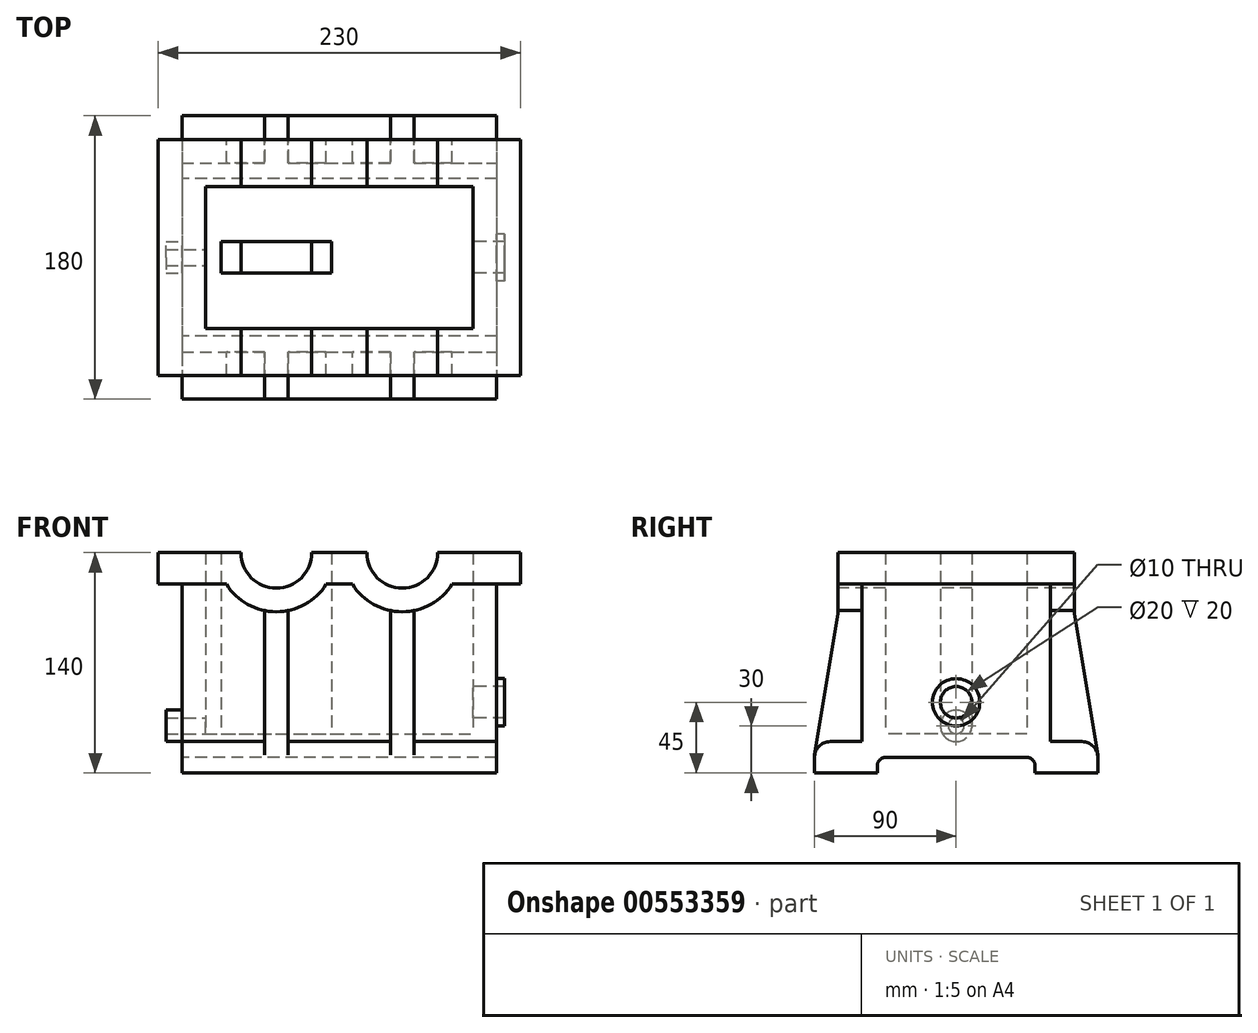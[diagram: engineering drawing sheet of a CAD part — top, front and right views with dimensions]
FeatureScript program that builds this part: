
annotation { "Feature Type Name" : "Feature", "Feature Type Description" : "" }
export const myFeature = defineFeature(function(context is Context, id is Id, definition is map)
    precondition{}
    {
        {
            var Q0;
            Q0=qCreatedBy(makeId("Top.planeOp"),FACE);
            var sketch = newSketch(context, id + "F0", { "sketchPlane" : qUnion([Q0])});
            skLineSegment(sketch, "E0.bottom", {"start": v(-100, 60) * mm, "end": v(100, 60) * mm});
            skLineSegment(sketch, "E0.top", {"start": v(-100, -60) * mm, "end": v(100, -60) * mm});
            skLineSegment(sketch, "E0.left", {"start": v(-100, 60) * mm, "end": v(-100, -60) * mm});
            skLineSegment(sketch, "E0.right", {"start": v(100, 60) * mm, "end": v(100, -60) * mm});
            skPoint(sketch, "E0.middle", {"position": v(0, 0) * mm});
            skSolve(sketch);
        }
        {
            var Q0;
            Q0=makeQuery(id+"F0.imprint","IMPRINT",FACE,{"disambiguationData":[TD([[makeQuery(id+"F0.imprint","IMPRINT",EDGE,{"derivedFrom":sQuery(id+"F0.wireOp",EDGE,"E0.bottom")}),-1.0]])]});
            extrude(context, id + "F1", {"entities" : qUnion([Q0]), "depth" : 100 * mm, "offsetDistance" : 25 * mm});
        }
        {
            var Q0;
            Q0=makeQuery(id+"F1.opExtrude","CAP_FACE",FACE,{"disambiguationData":[OSD([sQuery(id+"F0.wireOp",EDGE,"E0.bottom"),sQuery(id+"F0.wireOp",EDGE,"E0.top"),sQuery(id+"F0.wireOp",EDGE,"E0.left"),sQuery(id+"F0.wireOp",EDGE,"E0.right")])],"isStart":false});
            shell(context, id + "F2", {"entities" : qUnion([Q0]), "thickness" : 15 * mm});
        }
        {
            var Q0;
            Q0=makeQuery(id+"F1.opExtrude","CAP_FACE",FACE,{"disambiguationData":[OSD([sQuery(id+"F0.wireOp",EDGE,"E0.bottom"),sQuery(id+"F0.wireOp",EDGE,"E0.top"),sQuery(id+"F0.wireOp",EDGE,"E0.left"),sQuery(id+"F0.wireOp",EDGE,"E0.right")])],"isStart":false});
            var sketch = newSketch(context, id + "F3", { "sketchPlane" : qUnion([Q0])});
            skLineSegment(sketch, "E1.bottom", {"start": v(-115, 75) * mm, "end": v(115, 75) * mm});
            skLineSegment(sketch, "E1.top", {"start": v(-115, -75) * mm, "end": v(115, -75) * mm});
            skLineSegment(sketch, "E1.left", {"start": v(-115, 75) * mm, "end": v(-115, -75) * mm});
            skLineSegment(sketch, "E1.right", {"start": v(115, 75) * mm, "end": v(115, -75) * mm});
            skPoint(sketch, "E1.middle", {"position": v(0, 0) * mm});
            skLineSegment(sketch, "E2.0", {"start": v(-85, 45) * mm, "end": v(85, 45) * mm});
            skLineSegment(sketch, "E3.0", {"start": v(85, 45) * mm, "end": v(85, -45) * mm});
            skLineSegment(sketch, "E4.0", {"start": v(-85, -45) * mm, "end": v(85, -45) * mm});
            skLineSegment(sketch, "E5.0", {"start": v(-85, 45) * mm, "end": v(-85, -45) * mm});
            skSolve(sketch);
        }
        {
            var Q0;
            Q0 = qSketchRegion(id + "F3", true);
            extrude(context, id + "F4", {"entities" : qUnion([Q0]), "operationType" : NewBodyOperationType.ADD, "depth" : 20 * mm, "offsetDistance" : 25 * mm});
        }
        {
            var Q0;
            Q0=makeQuery(id+"F1.opExtrude","CAP_FACE",FACE,{"disambiguationData":[OSD([sQuery(id+"F0.wireOp",EDGE,"E0.bottom"),sQuery(id+"F0.wireOp",EDGE,"E0.top"),sQuery(id+"F0.wireOp",EDGE,"E0.left"),sQuery(id+"F0.wireOp",EDGE,"E0.right")])],"isStart":true});
            var sketch = newSketch(context, id + "F5", { "sketchPlane" : qUnion([Q0])});
            skLineSegment(sketch, "E6.bottom", {"start": v(-100, -90) * mm, "end": v(100, -90) * mm});
            skLineSegment(sketch, "E6.top", {"start": v(-100, 90) * mm, "end": v(100, 90) * mm});
            skLineSegment(sketch, "E6.left", {"start": v(-100, -90) * mm, "end": v(-100, 90) * mm});
            skLineSegment(sketch, "E6.right", {"start": v(100, -90) * mm, "end": v(100, 90) * mm});
            skPoint(sketch, "E6.middle", {"position": v(0, 0) * mm});
            skSolve(sketch);
        }
        {
            var Q0;
            Q0 = qSketchRegion(id + "F5", true);
            extrude(context, id + "F6", {"entities" : qUnion([Q0]), "operationType" : NewBodyOperationType.ADD, "depth" : 20 * mm, "offsetDistance" : 25 * mm});
        }
        {
            var Q0;
            Q0=makeQuery(id+"F6.boolean.opBoolean","MERGE",FACE,{"derivedFrom":[makeQuery(id+"F1.opExtrude","SWEPT_FACE",FACE,{"disambiguationData":[OSD([sQuery(id+"F0.wireOp",EDGE,"E0.left")])]}),makeQuery(id+"F6.opExtrude","SWEPT_FACE",FACE,{"disambiguationData":[OSD([sQuery(id+"F5.wireOp",EDGE,"E6.left")])]})]});
            var sketch = newSketch(context, id + "F7", { "sketchPlane" : qUnion([Q0])});
            skLineSegment(sketch, "E7.bottom", {"start": v(-50, -10) * mm, "end": v(50, -10) * mm});
            skLineSegment(sketch, "E7.top", {"start": v(-50, -20) * mm, "end": v(50, -20) * mm});
            skLineSegment(sketch, "E7.left", {"start": v(-50, -10) * mm, "end": v(-50, -20) * mm});
            skLineSegment(sketch, "E7.right", {"start": v(50, -10) * mm, "end": v(50, -20) * mm});
            skSolve(sketch);
        }
        {
            var Q0;
            Q0=makeQuery(id+"F7.imprint","IMPRINT",FACE,{"disambiguationData":[TD([[makeQuery(id+"F7.imprint","IMPRINT",EDGE,{"derivedFrom":sQuery(id+"F7.wireOp",EDGE,"E7.bottom")}),-1.0]])]});
            extrude(context, id + "F8", {"entities" : qUnion([Q0]), "operationType" : NewBodyOperationType.REMOVE, "oppositeDirection" : true, "depth" : 200 * mm, "offsetDistance" : 25 * mm});
        }
        {
            var Q0;
            Q0=makeQuery(id+"F8.boolean.opBoolean","COPY",EDGE,{"derivedFrom":makeQuery(id+"F8.opExtrude","SWEPT_EDGE",EDGE,{"disambiguationData":[OSD([sQuery(id+"F7.wireOp",EDGE,"E7.bottom"),sQuery(id+"F7.wireOp",EDGE,"E7.right")])]})});
            var Q1;
            Q1=makeQuery(id+"F8.boolean.opBoolean","COPY",EDGE,{"derivedFrom":makeQuery(id+"F8.opExtrude","SWEPT_EDGE",EDGE,{"disambiguationData":[OSD([sQuery(id+"F7.wireOp",EDGE,"E7.bottom"),sQuery(id+"F7.wireOp",EDGE,"E7.left")])]})});
            fillet(context, id + "F9", {"entities" : qUnion([Q0, Q1]), "radius" : 5 * mm, "tangentPropagation" : true, "allowEdgeOverflow" : false});
        }
        {
            var Q0;
            Q0=qCreatedBy(makeId("Front.planeOp"),FACE);
            var sketch = newSketch(context, id + "F10", { "sketchPlane" : qUnion([Q0])});
            skArc(sketch, "E8", {"start": v(-77.5, 120) * mm, "mid": v(-40, 82.5) * mm, "end": v(-2.5, 120) * mm});
            skArc(sketch, "E9", {"start": v(2.5, 120) * mm, "mid": v(40, 82.5) * mm, "end": v(77.5, 120) * mm});
            skLineSegment(sketch, "E10.0", {"start": v(-77.5, 120) * mm, "end": v(-2.5, 120) * mm});
            skPoint(sketch, "E11.orphan", {"position": v(-115, 120) * mm});
            skLineSegment(sketch, "E12.trimOffspring", {"start": v(2.5, 120) * mm, "end": v(77.5, 120) * mm});
            skPoint(sketch, "E13.orphan", {"position": v(115, 120) * mm});
            skSolve(sketch);
        }
        {
            var Q0;
            Q0 = qSketchRegion(id + "F10", true);
            var Q1;
            Q1=makeQuery(id+"F4.opExtrude","SWEPT_FACE",FACE,{"disambiguationData":[OSD([sQuery(id+"F3.wireOp",EDGE,"E1.top")])]});
            var Q2;
            Q2=makeQuery(id+"F4.opExtrude","SWEPT_FACE",FACE,{"disambiguationData":[OSD([sQuery(id+"F3.wireOp",EDGE,"E1.bottom")])]});
            extrude(context, id + "F11", {"entities" : qUnion([Q0]), "operationType" : NewBodyOperationType.ADD, "endBound" : BoundingType.UP_TO_SURFACE, "depth" : 25 * mm, "endBoundEntityFace" : qUnion([Q1]), "offsetDistance" : 25 * mm, "hasSecondDirection" : true, "secondDirectionBound" : SecondDirectionBoundingType.UP_TO_SURFACE, "secondDirectionOppositeDirection" : true, "secondDirectionDepth" : 25 * mm, "secondDirectionBoundEntityFace" : qUnion([Q2])});
        }
        {
            var Q0;
            Q0 = qSketchRegion(id + "F10", true);
            var Q1;
            Q1=makeQuery(id+"F4.boolean.opBoolean","MERGE",FACE,{"derivedFrom":[makeQuery(id+"F2.opShell","OFFSET_FACE",FACE,{"disambiguationData":[OSD([sQuery(id+"F0.wireOp",EDGE,"E0.top")])]}),makeQuery(id+"F4.opExtrude","SWEPT_FACE",FACE,{"disambiguationData":[OSD([sQuery(id+"F3.wireOp",EDGE,"E4.0")])]})]});
            var Q2;
            Q2=makeQuery(id+"F4.boolean.opBoolean","MERGE",FACE,{"derivedFrom":[makeQuery(id+"F2.opShell","OFFSET_FACE",FACE,{"disambiguationData":[OSD([sQuery(id+"F0.wireOp",EDGE,"E0.bottom")])]}),makeQuery(id+"F4.opExtrude","SWEPT_FACE",FACE,{"disambiguationData":[OSD([sQuery(id+"F3.wireOp",EDGE,"E2.0")])]})]});
            extrude(context, id + "F12", {"entities" : qUnion([Q0]), "operationType" : NewBodyOperationType.REMOVE, "endBound" : BoundingType.UP_TO_SURFACE, "depth" : 25 * mm, "endBoundEntityFace" : qUnion([Q1]), "offsetDistance" : 25 * mm, "hasSecondDirection" : true, "secondDirectionBound" : SecondDirectionBoundingType.UP_TO_SURFACE, "secondDirectionOppositeDirection" : true, "secondDirectionDepth" : 25 * mm, "secondDirectionBoundEntityFace" : qUnion([Q2])});
        }
        {
            var Q0;
            Q0=qCreatedBy(makeId("Front.planeOp"),FACE);
            var sketch = newSketch(context, id + "F13", { "sketchPlane" : qUnion([Q0])});
            skCircle(sketch, "E14", {"center": v(-40, 120) * mm, "radius": 22.5 * mm});
            skCircle(sketch, "E15", {"center": v(40, 120) * mm, "radius": 22.5 * mm});
            skSolve(sketch);
        }
        {
            var Q0;
            Q0 = qSketchRegion(id + "F13", true);
            extrude(context, id + "F14", {"entities" : qUnion([Q0]), "operationType" : NewBodyOperationType.REMOVE, "oppositeDirection" : true, "depth" : 200 * mm, "offsetDistance" : 25 * mm, "hasSecondDirection" : true, "secondDirectionOppositeDirection" : false, "secondDirectionDepth" : 200 * mm});
        }
        {
            var Q0;
            Q0=makeQuery(id+"F6.opExtrude","CAP_EDGE",EDGE,{"disambiguationData":[OSD([sQuery(id+"F5.wireOp",EDGE,"E6.top")])],"isStart":true});
            var Q1;
            Q1=makeQuery(id+"F6.opExtrude","CAP_EDGE",EDGE,{"disambiguationData":[OSD([sQuery(id+"F5.wireOp",EDGE,"E6.bottom")])],"isStart":true});
            fillet(context, id + "F15", {"entities" : qUnion([Q0, Q1]), "radius" : 10 * mm, "tangentPropagation" : true, "allowEdgeOverflow" : false});
        }
        {
            var Q0;
            Q0=qCreatedBy(makeId("Right.planeOp"),FACE);
            cPlane(context, id + "F16", {"entities" : qUnion([Q0]), "cplaneType" : CPlaneType.OFFSET, "offset" : 40 * mm, "width" : 150 * mm, "height" : 150 * mm});
        }
        {
            var Q0;
            Q0=qCreatedBy(makeId("Right.planeOp"),FACE);
            cPlane(context, id + "F17", {"entities" : qUnion([Q0]), "cplaneType" : CPlaneType.OFFSET, "offset" : 40 * mm, "oppositeDirection" : true, "width" : 150 * mm, "height" : 150 * mm});
        }
        {
            var Q0;
            Q0=qCreatedBy(id+"F16.planeOp",FACE);
            var sketch = newSketch(context, id + "F18", { "sketchPlane" : qUnion([Q0])});
            skLineSegment(sketch, "E16", {"start": v(72.14, 100) * mm, "end": v(89.87, -8.39) * mm});
            skLineSegment(sketch, "E17", {"start": v(60, -8.39) * mm, "end": v(60, 100) * mm});
            skLineSegment(sketch, "E18", {"start": v(60, 100) * mm, "end": v(72.14, 100) * mm});
            skLineSegment(sketch, "E19", {"start": v(60, -8.39) * mm, "end": v(89.87, -8.39) * mm});
            skLineSegment(sketch, "E20", {"start": v(60, 82.5) * mm, "end": v(75, 82.5) * mm});
            skLineSegment(sketch, "E21", {"start": v(0, 162.85) * mm, "end": v(0, -102.85) * mm, "construction": true});
            skLineSegment(sketch, "E22.MirrorCS", {"start": v(-72.14, 100) * mm, "end": v(-89.87, -8.39) * mm});
            skLineSegment(sketch, "E23.MirrorCS", {"start": v(-60, -8.39) * mm, "end": v(-89.87, -8.39) * mm});
            skLineSegment(sketch, "E24.MirrorCS", {"start": v(-60, -8.39) * mm, "end": v(-60, 100) * mm});
            skLineSegment(sketch, "E25.MirrorCS", {"start": v(-60, 100) * mm, "end": v(-72.14, 100) * mm});
            skSolve(sketch);
        }
        {
            var Q0;
            Q0 = qSketchRegion(id + "F18", true);
            extrude(context, id + "F19", {"entities" : qUnion([Q0]), "operationType" : NewBodyOperationType.ADD, "depth" : 7.5 * mm, "offsetDistance" : 25 * mm, "hasSecondDirection" : true, "secondDirectionOppositeDirection" : true, "secondDirectionDepth" : 7.5 * mm});
        }
        {
            var Q0;
            Q0=qCreatedBy(id+"F17.planeOp",FACE);
            var sketch = newSketch(context, id + "F20", { "sketchPlane" : qUnion([Q0])});
            skLineSegment(sketch, "E26.0", {"start": v(72.14, 100) * mm, "end": v(89.87, -8.39) * mm});
            skLineSegment(sketch, "E27.0", {"start": v(60, 100) * mm, "end": v(72.14, 100) * mm});
            skLineSegment(sketch, "E28.0", {"start": v(60, -8.39) * mm, "end": v(60, 100) * mm});
            skLineSegment(sketch, "E29.0", {"start": v(60, -8.39) * mm, "end": v(89.87, -8.39) * mm});
            skLineSegment(sketch, "E30.0", {"start": v(-60, -8.39) * mm, "end": v(-89.87, -8.39) * mm});
            skLineSegment(sketch, "E31.0", {"start": v(-60, -8.39) * mm, "end": v(-60, 100) * mm});
            skLineSegment(sketch, "E32.0", {"start": v(-72.14, 100) * mm, "end": v(-89.87, -8.39) * mm});
            skLineSegment(sketch, "E33.0", {"start": v(-60, 100) * mm, "end": v(-72.14, 100) * mm});
            skSolve(sketch);
        }
        {
            var Q0;
            Q0 = qSketchRegion(id + "F20", true);
            extrude(context, id + "F21", {"entities" : qUnion([Q0]), "operationType" : NewBodyOperationType.ADD, "depth" : 7.5 * mm, "offsetDistance" : 25 * mm, "hasSecondDirection" : true, "secondDirectionOppositeDirection" : true, "secondDirectionDepth" : 7.5 * mm});
        }
        {
            var Q0;
            Q0 = qSketchRegion(id + "F13", true);
            extrude(context, id + "F22", {"entities" : qUnion([Q0]), "operationType" : NewBodyOperationType.REMOVE, "oppositeDirection" : true, "depth" : 200 * mm, "offsetDistance" : 25 * mm, "hasSecondDirection" : true, "secondDirectionOppositeDirection" : false, "secondDirectionDepth" : 200 * mm});
        }
        {
            var Q0;
            Q0=makeQuery(id+"F2.opShell","OFFSET_FACE",FACE,{"disambiguationData":[OSD([sQuery(id+"F0.wireOp",EDGE,"E0.bottom"),sQuery(id+"F0.wireOp",EDGE,"E0.top"),sQuery(id+"F0.wireOp",EDGE,"E0.left"),sQuery(id+"F0.wireOp",EDGE,"E0.right")])]});
            extrude(context, id + "F23", {"entities" : qUnion([Q0]), "operationType" : NewBodyOperationType.REMOVE, "oppositeDirection" : true, "depth" : 10 * mm, "offsetDistance" : 25 * mm});
        }
        {
            var Q0;
            Q0=makeQuery(id+"F6.boolean.opBoolean","MERGE",FACE,{"derivedFrom":[makeQuery(id+"F1.opExtrude","SWEPT_FACE",FACE,{"disambiguationData":[OSD([sQuery(id+"F0.wireOp",EDGE,"E0.left")])]}),makeQuery(id+"F6.opExtrude","SWEPT_FACE",FACE,{"disambiguationData":[OSD([sQuery(id+"F5.wireOp",EDGE,"E6.left")])]})]});
            var sketch = newSketch(context, id + "F24", { "sketchPlane" : qUnion([Q0])});
            skCircle(sketch, "E34", {"center": v(0, 10) * mm, "radius": 5 * mm});
            skCircle(sketch, "E35", {"center": v(0, 10) * mm, "radius": 10 * mm});
            skLineSegment(sketch, "E36.0", {"start": v(-45, 5) * mm, "end": v(45, 5) * mm, "construction": true});
            skSolve(sketch);
        }
        {
            var Q0;
            Q0 = qSketchRegion(id + "F24", true);
            extrude(context, id + "F25", {"entities" : qUnion([Q0]), "operationType" : NewBodyOperationType.ADD, "depth" : 10 * mm, "offsetDistance" : 25 * mm});
        }
        {
            var Q0;
            Q0=makeQuery(id+"F25.boolean.opBoolean","SPLIT",FACE,{"disambiguationData":[TD([makeQuery(id+"F25.opExtrude","SWEPT_FACE",FACE,{"disambiguationData":[OSD([sQuery(id+"F24.wireOp",EDGE,"E34")])]})])],"derivedFrom":makeQuery(id+"F6.boolean.opBoolean","MERGE",FACE,{"derivedFrom":[makeQuery(id+"F1.opExtrude","SWEPT_FACE",FACE,{"disambiguationData":[OSD([sQuery(id+"F0.wireOp",EDGE,"E0.left")])]}),makeQuery(id+"F6.opExtrude","SWEPT_FACE",FACE,{"disambiguationData":[OSD([sQuery(id+"F5.wireOp",EDGE,"E6.left")])]})]})});
            extrude(context, id + "F26", {"entities" : qUnion([Q0]), "operationType" : NewBodyOperationType.REMOVE, "oppositeDirection" : true, "depth" : 25 * mm, "offsetDistance" : 25 * mm});
        }
        {
            var Q0;
            Q0=makeQuery(id+"F6.boolean.opBoolean","MERGE",FACE,{"derivedFrom":[makeQuery(id+"F1.opExtrude","SWEPT_FACE",FACE,{"disambiguationData":[OSD([sQuery(id+"F0.wireOp",EDGE,"E0.right")])]}),makeQuery(id+"F6.opExtrude","SWEPT_FACE",FACE,{"disambiguationData":[OSD([sQuery(id+"F5.wireOp",EDGE,"E6.right")])]})]});
            var sketch = newSketch(context, id + "F27", { "sketchPlane" : qUnion([Q0])});
            skCircle(sketch, "E37", {"center": v(0, 25) * mm, "radius": 15 * mm});
            skCircle(sketch, "E38", {"center": v(0, 25) * mm, "radius": 10 * mm});
            skLineSegment(sketch, "E39.0", {"start": v(45, 5) * mm, "end": v(0, 5) * mm, "construction": true});
            skSolve(sketch);
        }
        {
            var Q0;
            Q0 = qSketchRegion(id + "F27", true);
            extrude(context, id + "F28", {"entities" : qUnion([Q0]), "operationType" : NewBodyOperationType.ADD, "depth" : 5 * mm, "offsetDistance" : 25 * mm});
        }
        {
            var Q0;
            Q0=makeQuery(id+"F28.boolean.opBoolean","SPLIT",FACE,{"disambiguationData":[TD([makeQuery(id+"F28.opExtrude","SWEPT_FACE",FACE,{"disambiguationData":[OSD([sQuery(id+"F27.wireOp",EDGE,"E38")])]})])],"derivedFrom":makeQuery(id+"F6.boolean.opBoolean","MERGE",FACE,{"derivedFrom":[makeQuery(id+"F1.opExtrude","SWEPT_FACE",FACE,{"disambiguationData":[OSD([sQuery(id+"F0.wireOp",EDGE,"E0.right")])]}),makeQuery(id+"F6.opExtrude","SWEPT_FACE",FACE,{"disambiguationData":[OSD([sQuery(id+"F5.wireOp",EDGE,"E6.right")])]})]})});
            extrude(context, id + "F29", {"entities" : qUnion([Q0]), "operationType" : NewBodyOperationType.REMOVE, "oppositeDirection" : true, "depth" : 25 * mm, "offsetDistance" : 25 * mm});
        }
        {
            var Q0;
            Q0=makeQuery(id+"F23.boolean.opBoolean","COPY",FACE,{"derivedFrom":makeQuery(id+"F23.opExtrude","CAP_FACE",FACE,{"disambiguationData":[OSD([sQuery(id+"F0.wireOp",EDGE,"E0.bottom"),sQuery(id+"F0.wireOp",EDGE,"E0.top"),sQuery(id+"F0.wireOp",EDGE,"E0.left"),sQuery(id+"F0.wireOp",EDGE,"E0.right")])],"isStart":false})});
            var sketch = newSketch(context, id + "F30", { "sketchPlane" : qUnion([Q0])});
            skLineSegment(sketch, "E40.bottom", {"start": v(-75, 10) * mm, "end": v(-5, 10) * mm});
            skLineSegment(sketch, "E40.top", {"start": v(-75, -10) * mm, "end": v(-5, -10) * mm});
            skLineSegment(sketch, "E40.left", {"start": v(-5, 10) * mm, "end": v(-5, -10) * mm});
            skLineSegment(sketch, "E40.right", {"start": v(-75, 10) * mm, "end": v(-75, -10) * mm});
            skSolve(sketch);
        }
        {
            var Q0;
            Q0 = qSketchRegion(id + "F30", true);
            var Q1;
            {var subQ0=sQuery(id+"F3.wireOp",EDGE,"E2.0");var subQ1=sQuery(id+"F3.wireOp",EDGE,"E1.bottom");var subQ2=sQuery(id+"F0.wireOp",EDGE,"E0.bottom");Q1=makeQuery(id+"F14.boolean.opBoolean","SPLIT",FACE,{"disambiguationData":[TD([makeQuery(id+"F2.opShell","OFFSET_FACE",FACE,{"disambiguationData":[OSD([subQ2])]}),makeQuery(id+"F4.opExtrude","SWEPT_FACE",FACE,{"disambiguationData":[OSD([subQ1])]}),makeQuery(id+"F4.opExtrude","SWEPT_FACE",FACE,{"disambiguationData":[OSD([subQ0])]}),makeQuery(id+"F11.opExtrude","CAP_FACE",FACE,{"disambiguationData":[OSD([subQ1]),OD(0.0)],"isStart":true}),makeQuery(id+"F11.opExtrude","CAP_FACE",FACE,{"disambiguationData":[OSD([subQ1]),OD(1.0)],"isStart":true}),makeQuery(id+"F12.opExtrude","CAP_FACE",FACE,{"disambiguationData":[OSD([subQ2,subQ0]),OD(0.0)],"isStart":true}),makeQuery(id+"F12.opExtrude","CAP_FACE",FACE,{"disambiguationData":[OSD([subQ2,subQ0]),OD(1.0)],"isStart":true}),makeQuery(id+"F14.opExtrude","SWEPT_FACE",FACE,{"disambiguationData":[OSD([sQuery(id+"F13.wireOp",EDGE,"E14")])]}),makeQuery(id+"F14.opExtrude","SWEPT_FACE",FACE,{"disambiguationData":[OSD([sQuery(id+"F13.wireOp",EDGE,"E15")])]})])],"derivedFrom":makeQuery(id+"F11.boolean.opBoolean","MERGE",FACE,{"derivedFrom":[makeQuery(id+"F4.opExtrude","CAP_FACE",FACE,{"disambiguationData":[OSD([subQ1,sQuery(id+"F3.wireOp",EDGE,"E1.top"),sQuery(id+"F3.wireOp",EDGE,"E1.left"),sQuery(id+"F3.wireOp",EDGE,"E1.right"),subQ0,sQuery(id+"F3.wireOp",EDGE,"E3.0"),sQuery(id+"F3.wireOp",EDGE,"E4.0"),sQuery(id+"F3.wireOp",EDGE,"E5.0")])],"isStart":false}),makeQuery(id+"F11.opExtrude","SWEPT_FACE",FACE,{"disambiguationData":[OSD([sQuery(id+"F10.wireOp",EDGE,"E10.0")])]}),makeQuery(id+"F11.opExtrude","SWEPT_FACE",FACE,{"disambiguationData":[OSD([sQuery(id+"F10.wireOp",EDGE,"E12.trimOffspring")])]})]})});}
            extrude(context, id + "F31", {"entities" : qUnion([Q0]), "operationType" : NewBodyOperationType.ADD, "endBound" : BoundingType.UP_TO_SURFACE, "depth" : 25 * mm, "endBoundEntityFace" : qUnion([Q1]), "offsetDistance" : 25 * mm});
        }
        {
            var Q0;
            Q0 = qSketchRegion(id + "F13", true);
            extrude(context, id + "F32", {"entities" : qUnion([Q0]), "operationType" : NewBodyOperationType.REMOVE, "oppositeDirection" : true, "depth" : 25 * mm, "offsetDistance" : 25 * mm, "hasSecondDirection" : true, "secondDirectionOppositeDirection" : false, "secondDirectionDepth" : 25 * mm});
        }
    });
